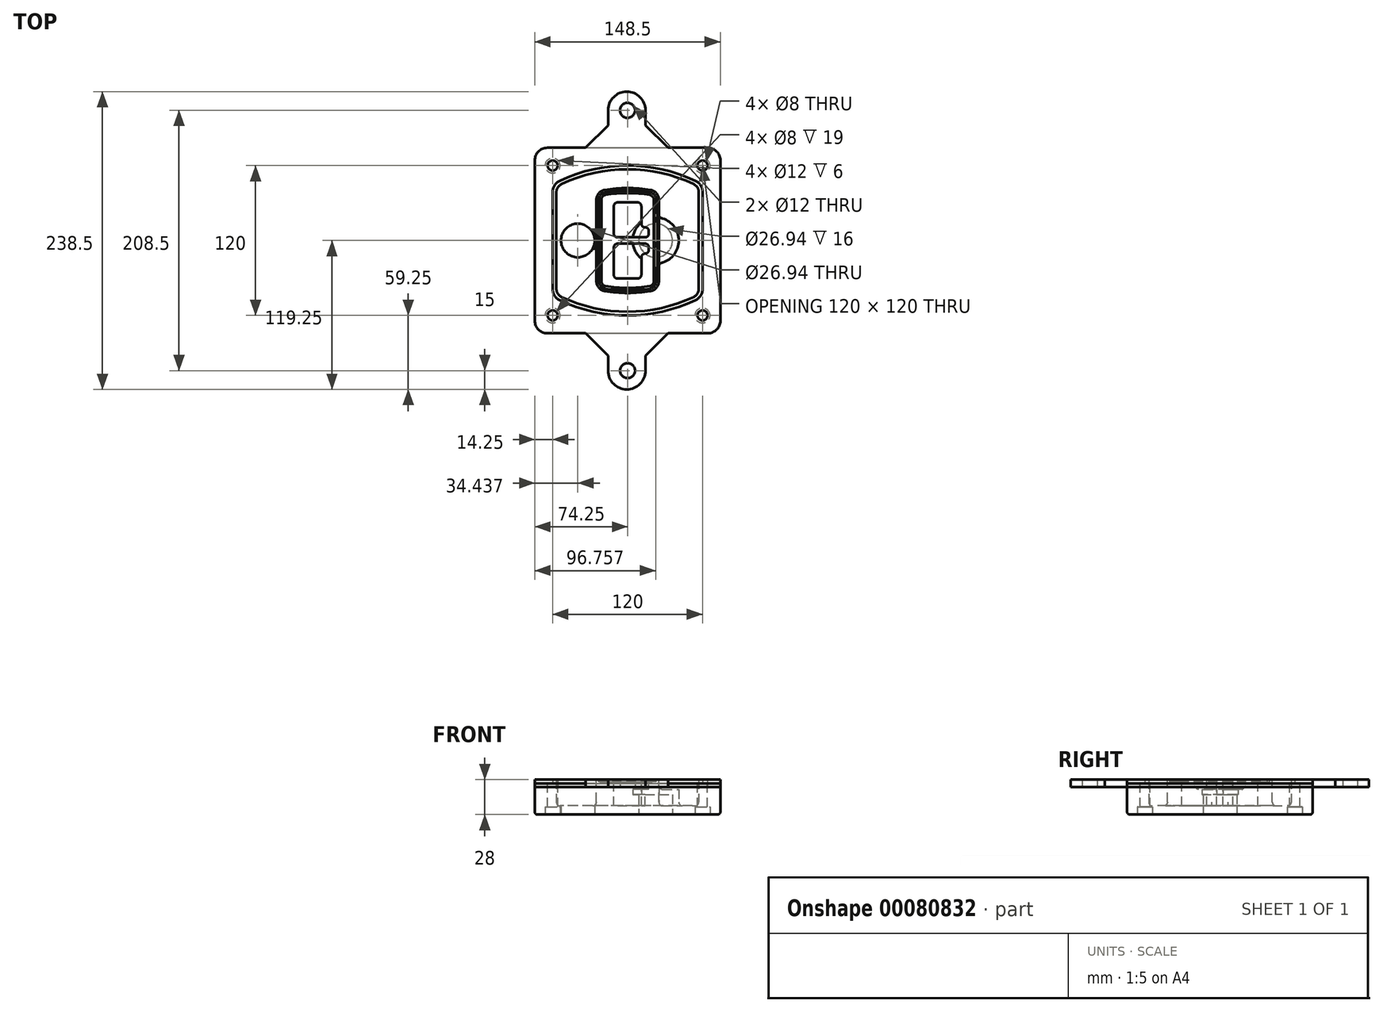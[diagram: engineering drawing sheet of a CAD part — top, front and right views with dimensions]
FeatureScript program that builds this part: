
annotation { "Feature Type Name" : "Feature", "Feature Type Description" : "" }
export const myFeature = defineFeature(function(context is Context, id is Id, definition is map)
    precondition{}
    {
        {
            var Q0;
            Q0=qCreatedBy(makeId("Top.planeOp"),FACE);
            var sketch = newSketch(context, id + "F0", { "sketchPlane" : qUnion([Q0])});
            skPoint(sketch, "E0.rect.middle", {"position": v(0, 0) * mm});
            skLineSegment(sketch, "E1.bottom", {"start": v(-64.25, -74.25) * mm, "end": v(64.25, -74.25) * mm});
            skLineSegment(sketch, "E1.top", {"start": v(-64.25, 74.25) * mm, "end": v(64.25, 74.25) * mm});
            skLineSegment(sketch, "E1.left", {"start": v(-74.25, -64.25) * mm, "end": v(-74.25, 64.25) * mm});
            skLineSegment(sketch, "E1.right", {"start": v(74.25, -64.25) * mm, "end": v(74.25, 64.25) * mm});
            skLineSegment(sketch, "E2", {"start": v(-74.25, 74.25) * mm, "end": v(74.25, -74.25) * mm, "construction": true});
            skLineSegment(sketch, "E3", {"start": v(74.25, 74.25) * mm, "end": v(-74.25, -74.25) * mm, "construction": true});
            skCircle(sketch, "E4", {"center": v(-60, 60) * mm, "radius": 4 * mm});
            skCircle(sketch, "E5", {"center": v(60, 60) * mm, "radius": 4 * mm});
            skCircle(sketch, "E6", {"center": v(60, -60) * mm, "radius": 4 * mm});
            skCircle(sketch, "E7", {"center": v(-60, -60) * mm, "radius": 4 * mm});
            skLineSegment(sketch, "E8", {"start": v(-60, 60) * mm, "end": v(60, 60) * mm, "construction": true});
            skLineSegment(sketch, "E9", {"start": v(60, 60) * mm, "end": v(60, -60) * mm, "construction": true});
            skLineSegment(sketch, "E10", {"start": v(60, -60) * mm, "end": v(-60, -60) * mm, "construction": true});
            skLineSegment(sketch, "E11", {"start": v(-60, -60) * mm, "end": v(-60, 60) * mm, "construction": true});
            skLineSegment(sketch, "E12", {"start": v(-60, 38.83) * mm, "end": v(-60, -38.83) * mm});
            skLineSegment(sketch, "E13", {"start": v(60, 38.83) * mm, "end": v(60, -38.83) * mm});
            skArc(sketch, "E14", {"start": v(54.26, 47.88) * mm, "mid": v(0, 60) * mm, "end": v(-54.26, 47.88) * mm});
            skArc(sketch, "E15", {"start": v(-54.26, -47.88) * mm, "mid": v(0, -60) * mm, "end": v(54.26, -47.88) * mm});
            skLineSegment(sketch, "E16", {"start": v(-60, 0) * mm, "end": v(60, 0) * mm, "construction": true});
            skPoint(sketch, "E17.visualSharp", {"position": v(-60, -45) * mm});
            skArc(sketch, "E17.filletArc", {"start": v(-60, -38.83) * mm, "mid": v(-58.44, -44.2) * mm, "end": v(-54.26, -47.88) * mm});
            skPoint(sketch, "E18.visualSharp", {"position": v(-60, 45) * mm});
            skArc(sketch, "E18.filletArc", {"start": v(-54.26, 47.88) * mm, "mid": v(-58.44, 44.2) * mm, "end": v(-60, 38.83) * mm});
            skPoint(sketch, "E19.visualSharp", {"position": v(60, 45) * mm});
            skArc(sketch, "E19.filletArc", {"start": v(60, 38.83) * mm, "mid": v(58.44, 44.2) * mm, "end": v(54.26, 47.88) * mm});
            skPoint(sketch, "E20.visualSharp", {"position": v(60, -45) * mm});
            skArc(sketch, "E20.filletArc", {"start": v(54.26, -47.88) * mm, "mid": v(58.44, -44.2) * mm, "end": v(60, -38.83) * mm});
            skPoint(sketch, "E21.visualSharp", {"position": v(-74.25, 74.25) * mm});
            skArc(sketch, "E21.filletArc", {"start": v(-64.25, 74.25) * mm, "mid": v(-71.32, 71.32) * mm, "end": v(-74.25, 64.25) * mm});
            skPoint(sketch, "E22.visualSharp", {"position": v(74.25, 74.25) * mm});
            skArc(sketch, "E22.filletArc", {"start": v(74.25, 64.25) * mm, "mid": v(71.32, 71.32) * mm, "end": v(64.25, 74.25) * mm});
            skPoint(sketch, "E23.visualSharp", {"position": v(74.25, -74.25) * mm});
            skArc(sketch, "E23.filletArc", {"start": v(64.25, -74.25) * mm, "mid": v(71.32, -71.32) * mm, "end": v(74.25, -64.25) * mm});
            skPoint(sketch, "E24.visualSharp", {"position": v(-74.25, -74.25) * mm});
            skArc(sketch, "E24.filletArc", {"start": v(-74.25, -64.25) * mm, "mid": v(-71.32, -71.32) * mm, "end": v(-64.25, -74.25) * mm});
            skArc(sketch, "E25.0", {"start": v(57, 38.83) * mm, "mid": v(55.9, 42.58) * mm, "end": v(52.98, 45.17) * mm});
            skLineSegment(sketch, "E25.1", {"start": v(57, 38.83) * mm, "end": v(57, -38.83) * mm});
            skArc(sketch, "E25.2", {"start": v(52.98, -45.17) * mm, "mid": v(55.9, -42.58) * mm, "end": v(57, -38.83) * mm});
            skArc(sketch, "E25.3", {"start": v(-52.98, -45.17) * mm, "mid": v(0, -57) * mm, "end": v(52.98, -45.17) * mm});
            skArc(sketch, "E25.4", {"start": v(-57, -38.83) * mm, "mid": v(-55.9, -42.58) * mm, "end": v(-52.98, -45.17) * mm});
            skArc(sketch, "E25.5", {"start": v(52.98, 45.17) * mm, "mid": v(0, 57) * mm, "end": v(-52.98, 45.17) * mm});
            skLineSegment(sketch, "E25.6", {"start": v(-57, 38.83) * mm, "end": v(-57, -38.83) * mm});
            skArc(sketch, "E25.7", {"start": v(-52.98, 45.17) * mm, "mid": v(-55.9, 42.58) * mm, "end": v(-57, 38.83) * mm});
            skArc(sketch, "E26.0", {"start": v(-55.96, 51.5) * mm, "mid": v(-61.82, 46.33) * mm, "end": v(-64, 38.83) * mm});
            skArc(sketch, "E26.1", {"start": v(55.96, 51.5) * mm, "mid": v(0, 64) * mm, "end": v(-55.96, 51.5) * mm});
            skArc(sketch, "E26.2", {"start": v(64, 38.83) * mm, "mid": v(61.82, 46.33) * mm, "end": v(55.96, 51.5) * mm});
            skLineSegment(sketch, "E26.3", {"start": v(64, 38.83) * mm, "end": v(64, -38.83) * mm});
            skArc(sketch, "E26.4", {"start": v(55.96, -51.5) * mm, "mid": v(61.82, -46.33) * mm, "end": v(64, -38.83) * mm});
            skLineSegment(sketch, "E26.5", {"start": v(-64, 38.83) * mm, "end": v(-64, -38.83) * mm});
            skArc(sketch, "E26.6", {"start": v(-55.96, -51.5) * mm, "mid": v(0, -64) * mm, "end": v(55.96, -51.5) * mm});
            skArc(sketch, "E26.7", {"start": v(-64, -38.83) * mm, "mid": v(-61.82, -46.33) * mm, "end": v(-55.96, -51.5) * mm});
            skSolve(sketch);
        }
        {
            var Q0;
            Q0=makeQuery(id+"F0.imprint","IMPRINT",FACE,{"disambiguationData":[TD([[makeQuery(id+"F0.imprint","IMPRINT",EDGE,{"derivedFrom":sQuery(id+"F0.wireOp",EDGE,"E1.bottom")}),1.0]])]});
            var Q1;
            Q1=makeQuery(id+"F0.imprint","IMPRINT",FACE,{"disambiguationData":[TD([[makeQuery(id+"F0.imprint","IMPRINT",EDGE,{"derivedFrom":sQuery(id+"F0.wireOp",EDGE,"E12")}),1.0]])]});
            var Q2;
            Q2=makeQuery(id+"F0.imprint","IMPRINT",FACE,{"disambiguationData":[TD([[makeQuery(id+"F0.imprint","IMPRINT",EDGE,{"derivedFrom":sQuery(id+"F0.wireOp",EDGE,"E25.0")}),1.0]])]});
            var Q3;
            Q3=makeQuery(id+"F0.imprint","IMPRINT",FACE,{"disambiguationData":[TD([[makeQuery(id+"F0.imprint","IMPRINT",EDGE,{"derivedFrom":sQuery(id+"F0.wireOp",EDGE,"E12")}),-1.0]])]});
            extrude(context, id + "F1", {"entities" : qUnion([Q0, Q1, Q2, Q3]), "oppositeDirection" : true, "depth" : 25 * mm});
        }
        {
            var Q0;
            Q0=makeQuery(id+"F0.imprint","IMPRINT",FACE,{"disambiguationData":[TD([[makeQuery(id+"F0.imprint","IMPRINT",EDGE,{"derivedFrom":sQuery(id+"F0.wireOp",EDGE,"E12")}),1.0]])]});
            extrude(context, id + "F2", {"entities" : qUnion([Q0]), "operationType" : NewBodyOperationType.ADD, "depth" : 3 * mm});
        }
        {
            var Q0;
            Q0=makeQuery(id+"F0.imprint","IMPRINT",FACE,{"disambiguationData":[TD([[makeQuery(id+"F0.imprint","IMPRINT",EDGE,{"derivedFrom":sQuery(id+"F0.wireOp",EDGE,"E25.0")}),1.0]])]});
            extrude(context, id + "F3", {"entities" : qUnion([Q0]), "operationType" : NewBodyOperationType.REMOVE, "oppositeDirection" : true, "depth" : 18 * mm});
        }
        {
            var Q0;
            Q0=makeQuery(id+"F2.opExtrude","CAP_FACE",FACE,{"disambiguationData":[OSD([sQuery(id+"F0.wireOp",EDGE,"E12"),sQuery(id+"F0.wireOp",EDGE,"E13"),sQuery(id+"F0.wireOp",EDGE,"E14"),sQuery(id+"F0.wireOp",EDGE,"E15"),sQuery(id+"F0.wireOp",EDGE,"E17.filletArc"),sQuery(id+"F0.wireOp",EDGE,"E18.filletArc"),sQuery(id+"F0.wireOp",EDGE,"E19.filletArc"),sQuery(id+"F0.wireOp",EDGE,"E20.filletArc"),sQuery(id+"F0.wireOp",EDGE,"E25.0"),sQuery(id+"F0.wireOp",EDGE,"E25.1"),sQuery(id+"F0.wireOp",EDGE,"E25.2"),sQuery(id+"F0.wireOp",EDGE,"E25.3"),sQuery(id+"F0.wireOp",EDGE,"E25.4"),sQuery(id+"F0.wireOp",EDGE,"E25.5"),sQuery(id+"F0.wireOp",EDGE,"E25.6"),sQuery(id+"F0.wireOp",EDGE,"E25.7")])],"isStart":false});
            var sketch = newSketch(context, id + "F4", { "sketchPlane" : qUnion([Q0])});
            skArc(sketch, "E27.0", {"start": v(-18.34, -40.45) * mm, "mid": v(0, -42) * mm, "end": v(18.34, -40.45) * mm});
            skArc(sketch, "E28.0", {"start": v(18.34, 40.45) * mm, "mid": v(0, 42) * mm, "end": v(-18.34, 40.45) * mm});
            skLineSegment(sketch, "E29", {"start": v(-25, 32.57) * mm, "end": v(-25, -32.57) * mm});
            skLineSegment(sketch, "E30", {"start": v(25, 32.57) * mm, "end": v(25, -32.57) * mm});
            skLineSegment(sketch, "E31", {"start": v(-25, 39.1) * mm, "end": v(25, 39.1) * mm, "construction": true});
            skLineSegment(sketch, "E32", {"start": v(-25, -39.1) * mm, "end": v(25, -39.1) * mm, "construction": true});
            skPoint(sketch, "E33.visualSharp", {"position": v(-25, 39.1) * mm});
            skArc(sketch, "E33.filletArc", {"start": v(-18.34, 40.45) * mm, "mid": v(-23.11, 37.73) * mm, "end": v(-25, 32.57) * mm});
            skPoint(sketch, "E34.visualSharp", {"position": v(25, 39.1) * mm});
            skArc(sketch, "E34.filletArc", {"start": v(25, 32.57) * mm, "mid": v(23.11, 37.73) * mm, "end": v(18.34, 40.45) * mm});
            skPoint(sketch, "E35.visualSharp", {"position": v(25, -39.1) * mm});
            skArc(sketch, "E35.filletArc", {"start": v(18.34, -40.45) * mm, "mid": v(23.11, -37.73) * mm, "end": v(25, -32.57) * mm});
            skPoint(sketch, "E36.visualSharp", {"position": v(-25, -39.1) * mm});
            skArc(sketch, "E36.filletArc", {"start": v(-25, -32.57) * mm, "mid": v(-23.11, -37.73) * mm, "end": v(-18.34, -40.45) * mm});
            skArc(sketch, "E37.0", {"start": v(52.98, 45.17) * mm, "mid": v(0, 57) * mm, "end": v(-52.98, 45.17) * mm});
            skArc(sketch, "E37.1", {"start": v(-52.98, 45.17) * mm, "mid": v(-55.9, 42.58) * mm, "end": v(-57, 38.83) * mm});
            skLineSegment(sketch, "E37.2", {"start": v(-57, 38.83) * mm, "end": v(-57, -38.83) * mm});
            skArc(sketch, "E37.3", {"start": v(-57, -38.83) * mm, "mid": v(-55.9, -42.58) * mm, "end": v(-52.98, -45.17) * mm});
            skArc(sketch, "E37.4", {"start": v(-52.98, -45.17) * mm, "mid": v(0, -57) * mm, "end": v(52.98, -45.17) * mm});
            skArc(sketch, "E37.5", {"start": v(52.98, -45.17) * mm, "mid": v(55.9, -42.58) * mm, "end": v(57, -38.83) * mm});
            skLineSegment(sketch, "E37.6", {"start": v(57, 38.83) * mm, "end": v(57, -38.83) * mm});
            skArc(sketch, "E37.7", {"start": v(57, 38.83) * mm, "mid": v(55.9, 42.58) * mm, "end": v(52.98, 45.17) * mm});
            skLineSegment(sketch, "E38.0", {"start": v(23, 32.57) * mm, "end": v(23, -32.57) * mm});
            skArc(sketch, "E38.1", {"start": v(18, -38.48) * mm, "mid": v(21.58, -36.44) * mm, "end": v(23, -32.57) * mm});
            skArc(sketch, "E38.2", {"start": v(-18, -38.48) * mm, "mid": v(0, -40) * mm, "end": v(18, -38.48) * mm});
            skArc(sketch, "E38.3", {"start": v(-23, -32.57) * mm, "mid": v(-21.58, -36.44) * mm, "end": v(-18, -38.48) * mm});
            skLineSegment(sketch, "E38.4", {"start": v(-23, 32.57) * mm, "end": v(-23, -32.57) * mm});
            skArc(sketch, "E38.5", {"start": v(23, 32.57) * mm, "mid": v(21.58, 36.44) * mm, "end": v(18, 38.48) * mm});
            skArc(sketch, "E38.6", {"start": v(-18, 38.48) * mm, "mid": v(-21.58, 36.44) * mm, "end": v(-23, 32.57) * mm});
            skArc(sketch, "E38.7", {"start": v(18, 38.48) * mm, "mid": v(0, 40) * mm, "end": v(-18, 38.48) * mm});
            skArc(sketch, "E39.0", {"start": v(21, 32.57) * mm, "mid": v(20.06, 35.15) * mm, "end": v(17.67, 36.5) * mm});
            skLineSegment(sketch, "E39.1", {"start": v(21, 32.57) * mm, "end": v(21, -32.57) * mm});
            skArc(sketch, "E39.2", {"start": v(17.67, -36.5) * mm, "mid": v(20.06, -35.15) * mm, "end": v(21, -32.57) * mm});
            skArc(sketch, "E39.3", {"start": v(-17.67, -36.5) * mm, "mid": v(0, -38) * mm, "end": v(17.67, -36.5) * mm});
            skArc(sketch, "E39.4", {"start": v(-21, -32.57) * mm, "mid": v(-20.06, -35.15) * mm, "end": v(-17.67, -36.5) * mm});
            skArc(sketch, "E39.5", {"start": v(17.67, 36.5) * mm, "mid": v(0, 38) * mm, "end": v(-17.67, 36.5) * mm});
            skLineSegment(sketch, "E39.6", {"start": v(-21, 32.57) * mm, "end": v(-21, -32.57) * mm});
            skArc(sketch, "E39.7", {"start": v(-17.67, 36.5) * mm, "mid": v(-20.06, 35.15) * mm, "end": v(-21, 32.57) * mm});
            skLineSegment(sketch, "E40", {"start": v(-25, 0) * mm, "end": v(25, 0) * mm, "construction": true});
            skLineSegment(sketch, "E41", {"start": v(-11, 5.5) * mm, "end": v(-11, 27.5) * mm});
            skLineSegment(sketch, "E42", {"start": v(-8, 30.5) * mm, "end": v(8, 30.5) * mm});
            skLineSegment(sketch, "E43", {"start": v(11, 27.5) * mm, "end": v(11, 13.5) * mm});
            skLineSegment(sketch, "E44", {"start": v(14, 10.5) * mm, "end": v(14, 10.5) * mm});
            skLineSegment(sketch, "E45", {"start": v(17, 7.5) * mm, "end": v(17, 5.5) * mm});
            skLineSegment(sketch, "E46", {"start": v(14, 2.5) * mm, "end": v(-8, 2.5) * mm});
            skPoint(sketch, "E47.visualSharp", {"position": v(-11, 30.5) * mm});
            skArc(sketch, "E47.filletArc", {"start": v(-8, 30.5) * mm, "mid": v(-10.12, 29.62) * mm, "end": v(-11, 27.5) * mm});
            skPoint(sketch, "E48.visualSharp", {"position": v(11, 30.5) * mm});
            skArc(sketch, "E48.filletArc", {"start": v(11, 27.5) * mm, "mid": v(10.12, 29.62) * mm, "end": v(8, 30.5) * mm});
            skPoint(sketch, "E49.visualSharp", {"position": v(11, 10.5) * mm});
            skArc(sketch, "E49.filletArc", {"start": v(11, 13.5) * mm, "mid": v(11.88, 11.38) * mm, "end": v(14, 10.5) * mm});
            skPoint(sketch, "E50.visualSharp", {"position": v(17, 10.5) * mm});
            skArc(sketch, "E50.filletArc", {"start": v(17, 7.5) * mm, "mid": v(16.12, 9.62) * mm, "end": v(14, 10.5) * mm});
            skPoint(sketch, "E51.visualSharp", {"position": v(17, 2.5) * mm});
            skArc(sketch, "E51.filletArc", {"start": v(14, 2.5) * mm, "mid": v(16.12, 3.38) * mm, "end": v(17, 5.5) * mm});
            skPoint(sketch, "E52.visualSharp", {"position": v(-11, 2.5) * mm});
            skArc(sketch, "E52.filletArc", {"start": v(-11, 5.5) * mm, "mid": v(-10.12, 3.38) * mm, "end": v(-8, 2.5) * mm});
            skLineSegment(sketch, "E53.0.MirrorCS", {"start": v(14, -2.5) * mm, "end": v(-8, -2.5) * mm});
            skArc(sketch, "E54.0.MirrorCS", {"start": v(-11, -5.5) * mm, "mid": v(-10.12, -3.38) * mm, "end": v(-8, -2.5) * mm});
            skLineSegment(sketch, "E55.0.MirrorCS", {"start": v(-11, -5.5) * mm, "end": v(-11, -27.5) * mm});
            skArc(sketch, "E56.0.MirrorCS", {"start": v(-8, -30.5) * mm, "mid": v(-10.12, -29.62) * mm, "end": v(-11, -27.5) * mm});
            skLineSegment(sketch, "E57.0.MirrorCS", {"start": v(-8, -30.5) * mm, "end": v(8, -30.5) * mm});
            skArc(sketch, "E58.0.MirrorCS", {"start": v(11, -27.5) * mm, "mid": v(10.12, -29.62) * mm, "end": v(8, -30.5) * mm});
            skLineSegment(sketch, "E59.0.MirrorCS", {"start": v(11, -27.5) * mm, "end": v(11, -13.5) * mm});
            skArc(sketch, "E60.0.MirrorCS", {"start": v(11, -13.5) * mm, "mid": v(11.88, -11.38) * mm, "end": v(14, -10.5) * mm});
            skArc(sketch, "E61.0.MirrorCS", {"start": v(17, -7.5) * mm, "mid": v(16.12, -9.62) * mm, "end": v(14, -10.5) * mm});
            skLineSegment(sketch, "E62.0.MirrorCS", {"start": v(17, -7.5) * mm, "end": v(17, -5.5) * mm});
            skArc(sketch, "E63.0.MirrorCS", {"start": v(14, -2.5) * mm, "mid": v(16.12, -3.38) * mm, "end": v(17, -5.5) * mm});
            skSolve(sketch);
        }
        {
            var Q0;
            Q0=makeQuery(id+"F4.imprint","IMPRINT",FACE,{"disambiguationData":[TD([[makeQuery(id+"F4.imprint","IMPRINT",EDGE,{"derivedFrom":sQuery(id+"F4.wireOp",EDGE,"E27.0")}),1.0]])]});
            var Q1;
            Q1=makeQuery(id+"F4.imprint","IMPRINT",FACE,{"disambiguationData":[TD([[makeQuery(id+"F4.imprint","IMPRINT",EDGE,{"derivedFrom":sQuery(id+"F4.wireOp",EDGE,"E38.0")}),-1.0]])]});
            var Q2;
            Q2=makeQuery(id+"F4.imprint","IMPRINT",FACE,{"disambiguationData":[TD([[makeQuery(id+"F4.imprint","IMPRINT",EDGE,{"derivedFrom":sQuery(id+"F4.wireOp",EDGE,"E39.0")}),1.0]])]});
            extrude(context, id + "F5", {"entities" : qUnion([Q0, Q1, Q2]), "operationType" : NewBodyOperationType.ADD, "endBound" : BoundingType.UP_TO_NEXT, "oppositeDirection" : true, "depth" : 25 * mm});
        }
        {
            var Q0;
            Q0=makeQuery(id+"F4.imprint","IMPRINT",FACE,{"disambiguationData":[TD([[makeQuery(id+"F4.imprint","IMPRINT",EDGE,{"derivedFrom":sQuery(id+"F4.wireOp",EDGE,"E38.0")}),-1.0]])]});
            extrude(context, id + "F6", {"entities" : qUnion([Q0]), "operationType" : NewBodyOperationType.REMOVE, "oppositeDirection" : true, "depth" : 2 * mm});
        }
        {
            var Q0;
            Q0=makeQuery(id+"F1.opExtrude","CAP_FACE",FACE,{"disambiguationData":[OSD([sQuery(id+"F0.wireOp",EDGE,"E1.bottom"),sQuery(id+"F0.wireOp",EDGE,"E1.top"),sQuery(id+"F0.wireOp",EDGE,"E1.left"),sQuery(id+"F0.wireOp",EDGE,"E1.right"),sQuery(id+"F0.wireOp",EDGE,"E4"),sQuery(id+"F0.wireOp",EDGE,"E5"),sQuery(id+"F0.wireOp",EDGE,"E6"),sQuery(id+"F0.wireOp",EDGE,"E7"),sQuery(id+"F0.wireOp",EDGE,"E21.filletArc"),sQuery(id+"F0.wireOp",EDGE,"E22.filletArc"),sQuery(id+"F0.wireOp",EDGE,"E23.filletArc"),sQuery(id+"F0.wireOp",EDGE,"E24.filletArc")])],"isStart":false});
            var sketch = newSketch(context, id + "F7", { "sketchPlane" : qUnion([Q0])});
            skCircle(sketch, "E64", {"center": v(22.5, 0) * mm, "radius": 13.47 * mm});
            skCircle(sketch, "E65", {"center": v(-39.81, 0) * mm, "radius": 13.47 * mm});
            skLineSegment(sketch, "E66", {"start": v(74.25, 0) * mm, "end": v(-74.25, 0) * mm});
            skCircle(sketch, "E67", {"center": v(22.5, 0) * mm, "radius": 18.47 * mm});
            skCircle(sketch, "E68", {"center": v(60, -60) * mm, "radius": 6 * mm});
            skCircle(sketch, "E69", {"center": v(-60, -60) * mm, "radius": 6 * mm});
            skCircle(sketch, "E70", {"center": v(-60, 60) * mm, "radius": 6 * mm});
            skCircle(sketch, "E71", {"center": v(60, 60) * mm, "radius": 6 * mm});
            skSolve(sketch);
        }
        {
            var Q0;
            {var subQ1=sQuery(id+"F7.wireOp",EDGE,"E66");var subQ4=sQuery(id+"F7.wireOp",EDGE,"E64");var subQ6=makeQuery(id+"F7.imprint","INTERSECT",VERTEX,{"disambiguationData":[OD(0.0)],"derivedFrom":[subQ4,subQ1]});Q0=makeQuery(id+"F7.imprint","IMPRINT",FACE,{"disambiguationData":[TD([[makeQuery(id+"F7.imprint","IMPRINT",EDGE,{"disambiguationData":[TD([[subQ6,-1.0]])],"derivedFrom":subQ4}),-1.0]])]});}
            var Q1;
            {var subQ0=sQuery(id+"F7.wireOp",EDGE,"E66");var subQ1=sQuery(id+"F7.wireOp",EDGE,"E64");var subQ3=makeQuery(id+"F7.imprint","INTERSECT",VERTEX,{"disambiguationData":[OD(0.0)],"derivedFrom":[subQ1,subQ0]});Q1=makeQuery(id+"F7.imprint","IMPRINT",FACE,{"disambiguationData":[TD([[makeQuery(id+"F7.imprint","IMPRINT",EDGE,{"disambiguationData":[TD([[subQ3,-1.0]])],"derivedFrom":subQ1}),1.0]])]});}
            var Q2;
            {var subQ0=sQuery(id+"F7.wireOp",EDGE,"E66");var subQ1=sQuery(id+"F7.wireOp",EDGE,"E64");var subQ3=makeQuery(id+"F7.imprint","INTERSECT",VERTEX,{"disambiguationData":[OD(0.0)],"derivedFrom":[subQ1,subQ0]});Q2=makeQuery(id+"F7.imprint","IMPRINT",FACE,{"disambiguationData":[TD([[makeQuery(id+"F7.imprint","IMPRINT",EDGE,{"disambiguationData":[TD([[subQ3,1.0]])],"derivedFrom":subQ1}),1.0]])]});}
            var Q3;
            {var subQ1=sQuery(id+"F7.wireOp",EDGE,"E66");var subQ4=sQuery(id+"F7.wireOp",EDGE,"E64");var subQ6=makeQuery(id+"F7.imprint","INTERSECT",VERTEX,{"disambiguationData":[OD(0.0)],"derivedFrom":[subQ4,subQ1]});Q3=makeQuery(id+"F7.imprint","IMPRINT",FACE,{"disambiguationData":[TD([[makeQuery(id+"F7.imprint","IMPRINT",EDGE,{"disambiguationData":[TD([[subQ6,1.0]])],"derivedFrom":subQ4}),-1.0]])]});}
            extrude(context, id + "F8", {"entities" : qUnion([Q0, Q1, Q2, Q3]), "operationType" : NewBodyOperationType.ADD, "oppositeDirection" : true, "depth" : 20 * mm});
        }
        {
            var Q0;
            {var subQ0=sQuery(id+"F7.wireOp",EDGE,"E66");var subQ1=sQuery(id+"F7.wireOp",EDGE,"E64");var subQ3=makeQuery(id+"F7.imprint","INTERSECT",VERTEX,{"disambiguationData":[OD(0.0)],"derivedFrom":[subQ1,subQ0]});Q0=makeQuery(id+"F7.imprint","IMPRINT",FACE,{"disambiguationData":[TD([[makeQuery(id+"F7.imprint","IMPRINT",EDGE,{"disambiguationData":[TD([[subQ3,-1.0]])],"derivedFrom":subQ1}),1.0]])]});}
            var Q1;
            {var subQ0=sQuery(id+"F7.wireOp",EDGE,"E66");var subQ1=sQuery(id+"F7.wireOp",EDGE,"E64");var subQ3=makeQuery(id+"F7.imprint","INTERSECT",VERTEX,{"disambiguationData":[OD(0.0)],"derivedFrom":[subQ1,subQ0]});Q1=makeQuery(id+"F7.imprint","IMPRINT",FACE,{"disambiguationData":[TD([[makeQuery(id+"F7.imprint","IMPRINT",EDGE,{"disambiguationData":[TD([[subQ3,1.0]])],"derivedFrom":subQ1}),1.0]])]});}
            extrude(context, id + "F9", {"entities" : qUnion([Q0, Q1]), "operationType" : NewBodyOperationType.REMOVE, "oppositeDirection" : true, "depth" : 16 * mm});
        }
        {
            var Q0;
            {var subQ0=sQuery(id+"F7.wireOp",EDGE,"E66");var subQ1=sQuery(id+"F7.wireOp",EDGE,"E65");var subQ3=makeQuery(id+"F7.imprint","INTERSECT",VERTEX,{"disambiguationData":[OD(0.0)],"derivedFrom":[subQ1,subQ0]});Q0=makeQuery(id+"F7.imprint","IMPRINT",FACE,{"disambiguationData":[TD([[makeQuery(id+"F7.imprint","IMPRINT",EDGE,{"disambiguationData":[TD([[subQ3,-1.0]])],"derivedFrom":subQ1}),1.0]])]});}
            var Q1;
            {var subQ0=sQuery(id+"F7.wireOp",EDGE,"E66");var subQ1=sQuery(id+"F7.wireOp",EDGE,"E65");var subQ3=makeQuery(id+"F7.imprint","INTERSECT",VERTEX,{"disambiguationData":[OD(0.0)],"derivedFrom":[subQ1,subQ0]});Q1=makeQuery(id+"F7.imprint","IMPRINT",FACE,{"disambiguationData":[TD([[makeQuery(id+"F7.imprint","IMPRINT",EDGE,{"disambiguationData":[TD([[subQ3,1.0]])],"derivedFrom":subQ1}),1.0]])]});}
            extrude(context, id + "F10", {"entities" : qUnion([Q0, Q1]), "operationType" : NewBodyOperationType.REMOVE, "oppositeDirection" : true, "depth" : 25 * mm});
        }
        {
            var Q0;
            Q0=makeQuery(id+"F7.imprint","IMPRINT",FACE,{"disambiguationData":[TD([[makeQuery(id+"F7.imprint","IMPRINT",EDGE,{"derivedFrom":sQuery(id+"F7.wireOp",EDGE,"E68")}),1.0]])]});
            var Q1;
            Q1=makeQuery(id+"F7.imprint","IMPRINT",FACE,{"disambiguationData":[TD([[makeQuery(id+"F7.imprint","IMPRINT",EDGE,{"derivedFrom":makeQuery(id+"F1.opExtrude","CAP_EDGE",EDGE,{"disambiguationData":[OSD([sQuery(id+"F0.wireOp",EDGE,"E5")])],"isStart":false})}),-1.0]])]});
            var Q2;
            Q2=makeQuery(id+"F7.imprint","IMPRINT",FACE,{"disambiguationData":[TD([[makeQuery(id+"F7.imprint","IMPRINT",EDGE,{"derivedFrom":sQuery(id+"F7.wireOp",EDGE,"E69")}),1.0]])]});
            var Q3;
            Q3=makeQuery(id+"F7.imprint","IMPRINT",FACE,{"disambiguationData":[TD([[makeQuery(id+"F7.imprint","IMPRINT",EDGE,{"derivedFrom":makeQuery(id+"F1.opExtrude","CAP_EDGE",EDGE,{"disambiguationData":[OSD([sQuery(id+"F0.wireOp",EDGE,"E4")])],"isStart":false})}),-1.0]])]});
            var Q4;
            Q4=makeQuery(id+"F7.imprint","IMPRINT",FACE,{"disambiguationData":[TD([[makeQuery(id+"F7.imprint","IMPRINT",EDGE,{"derivedFrom":sQuery(id+"F7.wireOp",EDGE,"E70")}),1.0]])]});
            var Q5;
            Q5=makeQuery(id+"F7.imprint","IMPRINT",FACE,{"disambiguationData":[TD([[makeQuery(id+"F7.imprint","IMPRINT",EDGE,{"derivedFrom":makeQuery(id+"F1.opExtrude","CAP_EDGE",EDGE,{"disambiguationData":[OSD([sQuery(id+"F0.wireOp",EDGE,"E7")])],"isStart":false})}),-1.0]])]});
            var Q6;
            Q6=makeQuery(id+"F7.imprint","IMPRINT",FACE,{"disambiguationData":[TD([[makeQuery(id+"F7.imprint","IMPRINT",EDGE,{"derivedFrom":sQuery(id+"F7.wireOp",EDGE,"E71")}),1.0]])]});
            var Q7;
            Q7=makeQuery(id+"F7.imprint","IMPRINT",FACE,{"disambiguationData":[TD([[makeQuery(id+"F7.imprint","IMPRINT",EDGE,{"derivedFrom":makeQuery(id+"F1.opExtrude","CAP_EDGE",EDGE,{"disambiguationData":[OSD([sQuery(id+"F0.wireOp",EDGE,"E6")])],"isStart":false})}),-1.0]])]});
            extrude(context, id + "F11", {"entities" : qUnion([Q0, Q1, Q2, Q3, Q4, Q5, Q6, Q7]), "operationType" : NewBodyOperationType.REMOVE, "oppositeDirection" : true, "depth" : 6 * mm});
        }
        {
            var Q0;
            Q0=makeQuery(id+"F9.boolean.opBoolean","COPY",FACE,{"derivedFrom":makeQuery(id+"F9.opExtrude","CAP_FACE",FACE,{"disambiguationData":[OSD([sQuery(id+"F7.wireOp",EDGE,"E64")])],"isStart":false})});
            var sketch = newSketch(context, id + "F12", { "sketchPlane" : qUnion([Q0])});
            skArc(sketch, "E72.0", {"start": v(11, 14.45) * mm, "mid": v(6.45, 9.13) * mm, "end": v(4.2, 2.5) * mm});
            skArc(sketch, "E72.1", {"start": v(4.2, -2.5) * mm, "mid": v(6.45, -9.13) * mm, "end": v(11, -14.45) * mm});
            skLineSegment(sketch, "E73", {"start": v(4.2, -2.5) * mm, "end": v(14, -2.5) * mm});
            skLineSegment(sketch, "E74.0", {"start": v(14, 2.5) * mm, "end": v(4.2, 2.5) * mm});
            skArc(sketch, "E74.1", {"start": v(14, 2.5) * mm, "mid": v(16.12, 3.38) * mm, "end": v(17, 5.5) * mm});
            skLineSegment(sketch, "E74.2", {"start": v(17, 7.5) * mm, "end": v(17, 5.5) * mm});
            skArc(sketch, "E74.3", {"start": v(17, 7.5) * mm, "mid": v(16.12, 9.62) * mm, "end": v(14, 10.5) * mm});
            skArc(sketch, "E74.4", {"start": v(11, 13.5) * mm, "mid": v(11.88, 11.38) * mm, "end": v(14, 10.5) * mm});
            skLineSegment(sketch, "E74.5", {"start": v(11, 14.45) * mm, "end": v(11, 13.5) * mm});
            skLineSegment(sketch, "E74.7", {"start": v(14, -2.5) * mm, "end": v(4.2, -2.5) * mm});
            skArc(sketch, "E74.8", {"start": v(14, -2.5) * mm, "mid": v(16.12, -3.38) * mm, "end": v(17, -5.5) * mm});
            skLineSegment(sketch, "E74.9", {"start": v(17, -7.5) * mm, "end": v(17, -5.5) * mm});
            skArc(sketch, "E74.10", {"start": v(17, -7.5) * mm, "mid": v(16.12, -9.62) * mm, "end": v(14, -10.5) * mm});
            skArc(sketch, "E74.11", {"start": v(11, -13.5) * mm, "mid": v(11.88, -11.38) * mm, "end": v(14, -10.5) * mm});
            skLineSegment(sketch, "E74.12", {"start": v(11, -14.45) * mm, "end": v(11, -13.5) * mm});
            skPoint(sketch, "E75.orphan", {"position": v(11, -27.5) * mm});
            skPoint(sketch, "E76.orphan", {"position": v(-8, -2.5) * mm});
            skPoint(sketch, "E77.orphan", {"position": v(-8, 2.5) * mm});
            skPoint(sketch, "E78.orphan", {"position": v(11, 27.5) * mm});
            skSolve(sketch);
        }
        {
            var Q0;
            {var subQ7=sQuery(id+"F12.wireOp",EDGE,"E72.0");var subQ14=sQuery(id+"F12.wireOp",EDGE,"E72.1");var subQ16=sQuery(id+"F12.wireOp",EDGE,"E74.1");var subQ18=sQuery(id+"F12.wireOp",EDGE,"E74.8");Q0=qUnion([makeQuery(id+"F12.imprint","IMPRINT",FACE,{"disambiguationData":[TD([[makeQuery(id+"F12.imprint","IMPRINT",EDGE,{"derivedFrom":subQ7}),1.0]])]}),makeQuery(id+"F12.imprint","IMPRINT",FACE,{"disambiguationData":[TD([[makeQuery(id+"F12.imprint","IMPRINT",EDGE,{"derivedFrom":subQ14}),1.0]])]}),makeQuery(id+"F12.imprint","IMPRINT",FACE,{"disambiguationData":[TD([[makeQuery(id+"F12.imprint","IMPRINT",EDGE,{"derivedFrom":subQ16}),1.0]])]}),makeQuery(id+"F12.imprint","IMPRINT",FACE,{"disambiguationData":[TD([[makeQuery(id+"F12.imprint","IMPRINT",EDGE,{"derivedFrom":subQ18}),-1.0]])]})]);}
            var Q1;
            Q1=makeQuery(id+"F5.boolean.opBoolean","SPLIT",FACE,{"disambiguationData":[TD([makeQuery(id+"F5.opExtrude","SWEPT_FACE",FACE,{"disambiguationData":[OSD([sQuery(id+"F4.wireOp",EDGE,"E41")])]})])],"derivedFrom":makeQuery(id+"F3.boolean.opBoolean","COPY",FACE,{"derivedFrom":makeQuery(id+"F3.opExtrude","CAP_FACE",FACE,{"disambiguationData":[OSD([sQuery(id+"F0.wireOp",EDGE,"E25.0"),sQuery(id+"F0.wireOp",EDGE,"E25.1"),sQuery(id+"F0.wireOp",EDGE,"E25.2"),sQuery(id+"F0.wireOp",EDGE,"E25.3"),sQuery(id+"F0.wireOp",EDGE,"E25.4"),sQuery(id+"F0.wireOp",EDGE,"E25.5"),sQuery(id+"F0.wireOp",EDGE,"E25.6"),sQuery(id+"F0.wireOp",EDGE,"E25.7")])],"isStart":false})})});
            extrude(context, id + "F13", {"entities" : qUnion([Q0]), "operationType" : NewBodyOperationType.REMOVE, "endBound" : BoundingType.UP_TO_SURFACE, "endBoundEntityFace" : qUnion([Q1]), "depth" : 25 * mm});
        }
        {
            var Q0;
            Q0=makeQuery(id+"F3.boolean.opBoolean","COPY",EDGE,{"derivedFrom":makeQuery(id+"F3.opExtrude","CAP_EDGE",EDGE,{"disambiguationData":[OSD([sQuery(id+"F0.wireOp",EDGE,"E25.6")])],"isStart":false})});
            var Q1;
            Q1=makeQuery(id+"F8.boolean.opBoolean","INTERSECT",EDGE,{"derivedFrom":[makeQuery(id+"F5.opExtrude","SWEPT_FACE",FACE,{"disambiguationData":[OSD([sQuery(id+"F4.wireOp",EDGE,"E30")])]}),makeQuery(id+"F8.opExtrude","CAP_FACE",FACE,{"disambiguationData":[OSD([sQuery(id+"F7.wireOp",EDGE,"E67")])],"isStart":false})]});
            var Q2;
            Q2=makeQuery(id+"F8.boolean.opBoolean","INTERSECT",EDGE,{"disambiguationData":[OD(1.0)],"derivedFrom":[makeQuery(id+"F5.opExtrude","SWEPT_FACE",FACE,{"disambiguationData":[OSD([sQuery(id+"F4.wireOp",EDGE,"E30")])]}),makeQuery(id+"F8.opExtrude","SWEPT_FACE",FACE,{"disambiguationData":[OSD([sQuery(id+"F7.wireOp",EDGE,"E67")])]})]});
            var Q3;
            {var subQ0=sQuery(id+"F4.wireOp",EDGE,"E30");Q3=makeQuery(id+"F8.boolean.opBoolean","SPLIT",EDGE,{"disambiguationData":[TD([makeQuery(id+"F5.opExtrude","SWEPT_FACE",FACE,{"disambiguationData":[OSD([sQuery(id+"F4.wireOp",EDGE,"E35.filletArc")])]})])],"derivedFrom":makeQuery(id+"F5.opExtrude","CAP_EDGE",EDGE,{"disambiguationData":[OSD([subQ0])],"isStart":false})});}
            var Q4;
            {var subQ0=sQuery(id+"F0.wireOp",EDGE,"E25.7");var subQ1=sQuery(id+"F0.wireOp",EDGE,"E25.1");var subQ2=sQuery(id+"F0.wireOp",EDGE,"E25.6");var subQ3=sQuery(id+"F0.wireOp",EDGE,"E25.5");var subQ4=sQuery(id+"F0.wireOp",EDGE,"E25.4");var subQ5=sQuery(id+"F0.wireOp",EDGE,"E25.0");var subQ6=sQuery(id+"F0.wireOp",EDGE,"E25.2");var subQ7=sQuery(id+"F0.wireOp",EDGE,"E25.3");Q4=makeQuery(id+"F8.boolean.opBoolean","INTERSECT",EDGE,{"derivedFrom":[makeQuery(id+"F5.boolean.opBoolean","SPLIT",FACE,{"disambiguationData":[TD([makeQuery(id+"F2.opExtrude","SWEPT_FACE",FACE,{"disambiguationData":[OSD([subQ5])]})])],"derivedFrom":makeQuery(id+"F3.boolean.opBoolean","COPY",FACE,{"derivedFrom":makeQuery(id+"F3.opExtrude","CAP_FACE",FACE,{"disambiguationData":[OSD([subQ5,subQ1,subQ6,subQ7,subQ4,subQ3,subQ2,subQ0])],"isStart":false})})}),makeQuery(id+"F8.opExtrude","SWEPT_FACE",FACE,{"disambiguationData":[OSD([sQuery(id+"F7.wireOp",EDGE,"E67")])]})]});}
            var Q5;
            Q5=makeQuery(id+"F8.boolean.opBoolean","INTERSECT",EDGE,{"disambiguationData":[OD(0.0)],"derivedFrom":[makeQuery(id+"F5.opExtrude","SWEPT_FACE",FACE,{"disambiguationData":[OSD([sQuery(id+"F4.wireOp",EDGE,"E30")])]}),makeQuery(id+"F8.opExtrude","SWEPT_FACE",FACE,{"disambiguationData":[OSD([sQuery(id+"F7.wireOp",EDGE,"E67")])]})]});
            fillet(context, id + "F14", {"entities" : qUnion([Q0, Q1, Q2, Q3, Q4, Q5]), "radius" : 3 * mm, "tangentPropagation" : true, "allowEdgeOverflow" : false});
        }
        {
            var Q0;
            Q0=makeQuery(id+"F1.opExtrude","CAP_EDGE",EDGE,{"disambiguationData":[OSD([sQuery(id+"F0.wireOp",EDGE,"E1.bottom")])],"isStart":false});
            fillet(context, id + "F15", {"entities" : qUnion([Q0]), "radius" : 2 * mm, "tangentPropagation" : true, "allowEdgeOverflow" : false});
        }
        {
            var Q0;
            {var subQ0=sQuery(id+"F0.wireOp",EDGE,"E22.filletArc");var subQ1=sQuery(id+"F0.wireOp",EDGE,"E7");var subQ2=sQuery(id+"F0.wireOp",EDGE,"E6");var subQ3=sQuery(id+"F0.wireOp",EDGE,"E5");var subQ4=sQuery(id+"F0.wireOp",EDGE,"E4");var subQ5=sQuery(id+"F0.wireOp",EDGE,"E1.bottom");var subQ6=sQuery(id+"F0.wireOp",EDGE,"E21.filletArc");var subQ7=sQuery(id+"F0.wireOp",EDGE,"E1.top");var subQ8=sQuery(id+"F0.wireOp",EDGE,"E1.left");var subQ9=sQuery(id+"F0.wireOp",EDGE,"E1.right");var subQ10=sQuery(id+"F0.wireOp",EDGE,"E23.filletArc");var subQ11=sQuery(id+"F0.wireOp",EDGE,"E24.filletArc");Q0=makeQuery(id+"F2.boolean.opBoolean","SPLIT",FACE,{"disambiguationData":[TD([makeQuery(id+"F1.opExtrude","SWEPT_FACE",FACE,{"disambiguationData":[OSD([subQ5])]})])],"derivedFrom":makeQuery(id+"F1.opExtrude","CAP_FACE",FACE,{"disambiguationData":[OSD([subQ5,subQ7,subQ8,subQ9,subQ4,subQ3,subQ2,subQ1,subQ6,subQ0,subQ10,subQ11])],"isStart":true})});}
            var sketch = newSketch(context, id + "F16", { "sketchPlane" : qUnion([Q0])});
            skLineSegment(sketch, "E79", {"start": v(0, 74.25) * mm, "end": v(0, 104.25) * mm, "construction": true});
            skCircle(sketch, "E80", {"center": v(0, 104.25) * mm, "radius": 6 * mm});
            skLineSegment(sketch, "E81", {"start": v(-15.62, 92.25) * mm, "end": v(-15.62, 104.25) * mm});
            skArc(sketch, "E82", {"start": v(0, 119.24) * mm, "mid": v(-11, 115.07) * mm, "end": v(-15.62, 104.25) * mm});
            skLineSegment(sketch, "E83", {"start": v(32.38, 74.25) * mm, "end": v(14.38, 92.25) * mm});
            skLineSegment(sketch, "E84", {"start": v(14.38, 92.25) * mm, "end": v(14.38, 104.25) * mm});
            skArc(sketch, "E85", {"start": v(14.38, 104.25) * mm, "mid": v(10.2, 114.64) * mm, "end": v(0, 119.24) * mm});
            skLineSegment(sketch, "E86", {"start": v(-74.25, 0) * mm, "end": v(74.25, 0) * mm, "construction": true});
            skLineSegment(sketch, "E87.MirrorCS", {"start": v(74.25, 0) * mm, "end": v(-74.25, 0) * mm, "construction": true});
            skLineSegment(sketch, "E88.MirrorCS", {"start": v(0, -74.25) * mm, "end": v(0, -104.25) * mm, "construction": true});
            skCircle(sketch, "E89.MirrorC", {"center": v(0, -104.25) * mm, "radius": 6 * mm});
            skLineSegment(sketch, "E90", {"start": v(-15.62, 92.25) * mm, "end": v(-33.62, 74.25) * mm});
            skLineSegment(sketch, "E91", {"start": v(-33.62, 74.25) * mm, "end": v(32.38, 74.25) * mm});
            skLineSegment(sketch, "E92.MirrorCS", {"start": v(-15.62, -92.25) * mm, "end": v(-33.62, -74.25) * mm});
            skLineSegment(sketch, "E93.MirrorCS", {"start": v(-15.62, -92.25) * mm, "end": v(-15.62, -104.25) * mm});
            skArc(sketch, "E94.MirrorCS", {"start": v(0, -119.24) * mm, "mid": v(-11, -115.07) * mm, "end": v(-15.62, -104.25) * mm});
            skArc(sketch, "E95.MirrorCS", {"start": v(14.38, -104.25) * mm, "mid": v(10.2, -114.64) * mm, "end": v(0, -119.24) * mm});
            skLineSegment(sketch, "E96.MirrorCS", {"start": v(14.38, -92.25) * mm, "end": v(14.38, -104.25) * mm});
            skLineSegment(sketch, "E97.MirrorCS", {"start": v(32.38, -74.25) * mm, "end": v(14.38, -92.25) * mm});
            skLineSegment(sketch, "E98.MirrorCS", {"start": v(-33.62, -74.25) * mm, "end": v(32.38, -74.25) * mm});
            skSolve(sketch);
        }
        {
            var Q0;
            {var subQ6=sQuery(id+"F16.wireOp",EDGE,"E91");Q0=makeQuery(id+"F16.imprint","IMPRINT",FACE,{"disambiguationData":[TD([[makeQuery(id+"F16.imprint","IMPRINT",EDGE,{"derivedFrom":subQ6}),-1.0]])]});}
            var Q1;
            Q1 = qSketchRegion(id + "F16", true);
            extrude(context, id + "F17", {"entities" : qUnion([Q0, Q1]), "endBound" : BoundingType.SYMMETRIC, "depth" : 6 * mm});
        }
    });
